# Revit family: ADLR-235-xxx-8xx-SMTx
name_source: partatom
category: Oprawy oświetleniowe
revit_build: Autodesk Revit 2017 (Build: 20190507_1515(x64)
units: mm (PartAtom-declared; Revit-internal decimal feet)

## family parameters
Numer OmniClass = 23.80.70.11
Obiekt nadrzędny = Powierzchnia
Punkt obliczania pomieszczeń = Nie
Tnij formami wycięć po wczytaniu = Nie
Typ części = Normalny
Tytuł OmniClass = Luminaries for Internal Lighting
Współdzielony = Nie
Wymiar okrągłego złącza = Użyj średnicy
Źródło światła = Tak

## types (12) — shared parameters
Emituj kształt widoczny w renderingu = Nie
Emituj ze średnicy okręgu = 210 mm  [stored 0.688976 ft]
Filtr koloru = 16777215
Kod zespołu = D5020200
Lampa = LED
Odchylenie kierunku = 90.00°
Producent = RIDI Leuchten GmbH
URL = www.ridi.de
Zmiana temperatury barwowej przyciemniania lampy = <Brak>
brand = RIDI
conformity mark = CE
electrical safety class = 1
height = 228 mm  [stored 0.748031 ft]
ingress protection (IP) code = IP40
length = 235 mm  [stored 0.770997 ft]
nominal frequency = 50-60Hz
nominal voltage = 230
voltage type (AC, DC, UC) = AC
weight = 3.56 kg
width = 235 mm  [stored 0.770997 ft]
zero-valued in all types: Domyślna rzędna

## per-type parameters (varying)
| type | Model | Obciążenie pozorne | Plik sieci fotometrycznej | product name | rated input power |
| ADLR 235/2000-830 SMT | 0321927 | 16 VA | ADLR 2352000-840 SMT.IES | ADLR 235/4000-840 W-DALI | 16 |
| ADLR 235/2000-830 SMT-DALI | 0331927 | 16 VA | ADLR 2352000-840 SMT.IES | ADLR 235/2000-830 SMT-DALI | 16 |
| ADLR 235/2000-840 SMT | 0321928 | 16 VA | ADLR 2352000-840 SMT.IES | ADLR 235/2000-840 SMT | 16 |
| ADLR 235/2000-840 SMT-DALI | 0331928 | 16 VA | ADLR 2352000-840 SMT.IES | ADLR 235/2000-840 SMT-DALI | 16 |
| ADLR 235/3000-830 SMT | 0321929 | 23 VA | ADLR 2353000-840 SMT.IES | ADLR 235/3000-830 SMT | 23 |
| ADLR 235/3000-830 SMT-DALI | 0331929 | 23 VA | ADLR 2353000-840 SMT.IES | ADLR 235/3000-830 SMT-DALI | 23 |
| ADLR 235/3000-840 SMT | 0321930 | 23 VA | ADLR 2353000-840 SMT.IES | ADLR 235/3000-840 SMT | 23 |
| ADLR 235/3000-840 SMT-DALI | 0331930 | 23 VA | ADLR 2353000-840 SMT.IES | ADLR 235/3000-840 SMT-DALI | 23 |
| ADLR 235/4000-830 SMT | 0322032 | 31 VA | ADLR 2354000-840 SMT.IES | ADLR 235/4000-830 SMT | 31 |
| ADLR 235/4000-830 SMT-DALI | 0332032 | 31 VA | ADLR 2354000-840 SMT.IES | ADLR 235/4000-830 SMT-DALI | 31 |
| ADLR 235/4000-840 SMT | 0322035 | 31 VA | ADLR 2354000-840 SMT.IES | ADLR 235/4000-840 SMT | 31 |
| ADLR 235/4000-840 SMT-DALI | 0332035 | 31 VA | ADLR 2354000-840 SMT.IES | ADLR 235/4000-840 SMT-DALI | 31 |

note: [stored X ft] marks values corroborated as IEEE doubles in the binary element streams (Revit-internal decimal feet)
